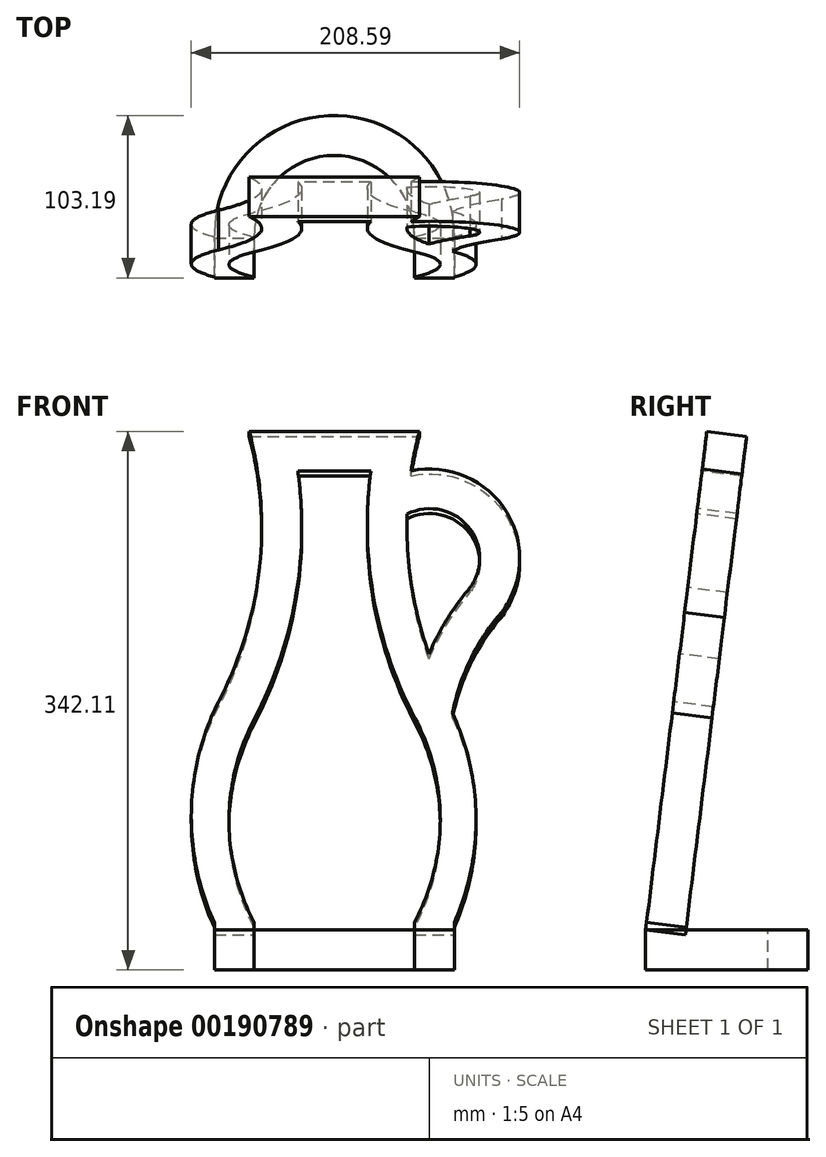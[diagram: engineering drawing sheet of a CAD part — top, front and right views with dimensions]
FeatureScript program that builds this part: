
annotation { "Feature Type Name" : "Feature", "Feature Type Description" : "" }
export const myFeature = defineFeature(function(context is Context, id is Id, definition is map)
    precondition{}
    {
        {
            var Q0;
            Q0=qCreatedBy(makeId("Top.planeOp"),FACE);
            var sketch = newSketch(context, id + "F0", { "sketchPlane" : qUnion([Q0])});
            skLineSegment(sketch, "E0", {"start": v(0, 0) * mm, "end": v(-62.54, 0) * mm});
            skSolve(sketch);
        }
        {
            var Q0;
            Q0=sQuery(id+"F0.wireOp",EDGE,"E0");
            var Q1;
            Q1=qCreatedBy(makeId("Front.planeOp"),FACE);
            cPlane(context, id + "F1", {"entities" : qUnion([Q0, Q1]), "cplaneType" : CPlaneType.LINE_ANGLE, "offset" : 25.4 * mm, "angle" : 7 * degree, "width" : 152.4 * mm, "height" : 152.4 * mm});
        }
        {
            var Q0;
            Q0=qCreatedBy(makeId("Top.planeOp"),FACE);
            cPlane(context, id + "F2", {"entities" : qUnion([Q0]), "cplaneType" : CPlaneType.OFFSET, "offset" : 0 * mm, "oppositeDirection" : true, "width" : 152.4 * mm, "height" : 152.4 * mm});
        }
        {
            var Q0;
            Q0=qCreatedBy(id+"F2.planeOp",FACE);
            var sketch = newSketch(context, id + "F3", { "sketchPlane" : qUnion([Q0])});
            skLineSegment(sketch, "E1", {"start": v(121.8, 0) * mm, "end": v(-111.18, 0) * mm, "construction": true});
            skLineSegment(sketch, "E2", {"start": v(0, 63.15) * mm, "end": v(0, -67.5) * mm, "construction": true});
            skLineSegment(sketch, "E3.bottom", {"start": v(-76.2, 0) * mm, "end": v(76.2, 0) * mm, "construction": true});
            skLineSegment(sketch, "E3.top", {"start": v(-76.2, 26.99) * mm, "end": v(76.2, 26.99) * mm, "construction": true});
            skLineSegment(sketch, "E3.left", {"start": v(-76.2, 0) * mm, "end": v(-76.2, 26.99) * mm});
            skLineSegment(sketch, "E3.right", {"start": v(76.2, 0) * mm, "end": v(76.2, 26.99) * mm});
            skPoint(sketch, "E4", {"position": v(0, 26.99) * mm});
            skLineSegment(sketch, "E5", {"start": v(-76.2, 0) * mm, "end": v(-50.8, 0) * mm});
            skLineSegment(sketch, "E6", {"start": v(-50.8, 0) * mm, "end": v(-50.8, 26.99) * mm});
            skLineSegment(sketch, "E7", {"start": v(76.2, 0) * mm, "end": v(50.8, 0) * mm});
            skLineSegment(sketch, "E8", {"start": v(50.8, 0) * mm, "end": v(50.8, 26.99) * mm});
            skArc(sketch, "E9", {"start": v(-50.8, 26.99) * mm, "mid": v(0, 77.79) * mm, "end": v(50.8, 26.99) * mm});
            skArc(sketch, "E10", {"start": v(-76.2, 26.99) * mm, "mid": v(0, 103.19) * mm, "end": v(76.2, 26.99) * mm});
            skSolve(sketch);
        }
        {
            var Q0;
            Q0=qSketchRegion(id+"F3",true);
            extrude(context, id + "F4", {"entities" : qUnion([Q0]), "oppositeDirection" : true, "depth" : 25.4 * mm});
        }
        {
            var Q0;
            Q0=qCreatedBy(id+"F1.planeOp",FACE);
            var sketch = newSketch(context, id + "F5", { "sketchPlane" : qUnion([Q0])});
            skArc(sketch, "E11", {"start": v(-63.5, 4.76) * mm, "mid": v(-78.79, 73.23) * mm, "end": v(-61.79, 141.29) * mm, "construction": true});
            skArc(sketch, "E12", {"start": v(-61.79, 141.29) * mm, "mid": v(-36, 221.84) * mm, "end": v(-38.1, 306.39) * mm, "construction": true});
            skLineSegment(sketch, "E13", {"start": v(-38.1, 306.39) * mm, "end": v(0, 306.39) * mm, "construction": true});
            skArc(sketch, "E14", {"start": v(-33.98, 274.64) * mm, "mid": v(-92.13, 270.54) * mm, "end": v(-96.22, 212.4) * mm, "construction": true});
            skLineSegment(sketch, "E15", {"start": v(-41.84, 266.78) * mm, "end": v(-126, 182.62) * mm, "construction": true});
            skArc(sketch, "E16", {"start": v(-96.22, 212.4) * mm, "mid": v(-74.32, 179.11) * mm, "end": v(-61.79, 141.29) * mm, "construction": true});
            skLineSegment(sketch, "E17.MirrorCS", {"start": v(38.1, 306.39) * mm, "end": v(0, 306.39) * mm, "construction": true});
            skArc(sketch, "E18.MirrorCS", {"start": v(61.79, 141.29) * mm, "mid": v(36, 221.84) * mm, "end": v(38.1, 306.39) * mm, "construction": true});
            skArc(sketch, "E19.MirrorCS", {"start": v(63.5, 4.76) * mm, "mid": v(78.79, 73.23) * mm, "end": v(61.79, 141.29) * mm, "construction": true});
            skArc(sketch, "E20.0", {"start": v(-76.2, 4.76) * mm, "mid": v(-90.04, 71.91) * mm, "end": v(-75.1, 138.83) * mm});
            skArc(sketch, "E20.1", {"start": v(-60.2, 176.74) * mm, "mid": v(-49, 220.83) * mm, "end": v(-46.27, 266.24) * mm});
            skArc(sketch, "E20.2", {"start": v(76.2, 4.76) * mm, "mid": v(90.8, 75.66) * mm, "end": v(73.66, 145.99) * mm});
            skArc(sketch, "E20.3", {"start": v(73.66, 145.99) * mm, "mid": v(47.67, 230.7) * mm, "end": v(54.02, 319.09) * mm});
            skLineSegment(sketch, "E20.4", {"start": v(54.02, 319.09) * mm, "end": v(0, 319.09) * mm});
            skLineSegment(sketch, "E20.5", {"start": v(-54.02, 319.09) * mm, "end": v(0, 319.09) * mm});
            skArc(sketch, "E21.0", {"start": v(-50.8, 4.76) * mm, "mid": v(-67.3, 70.02) * mm, "end": v(-51.37, 135.42) * mm});
            skArc(sketch, "E21.1", {"start": v(-51.37, 135.42) * mm, "mid": v(-25.08, 212.38) * mm, "end": v(-23.21, 293.69) * mm});
            skArc(sketch, "E21.2", {"start": v(50.8, 4.76) * mm, "mid": v(66.87, 69.44) * mm, "end": v(51.16, 134.2) * mm});
            skArc(sketch, "E21.3", {"start": v(51.16, 134.2) * mm, "mid": v(24.75, 211.77) * mm, "end": v(23.14, 293.69) * mm});
            skLineSegment(sketch, "E21.4", {"start": v(23.14, 293.69) * mm, "end": v(0, 293.69) * mm});
            skLineSegment(sketch, "E21.5", {"start": v(-23.21, 293.69) * mm, "end": v(0, 293.69) * mm});
            skArc(sketch, "E22.0", {"start": v(-106.05, 203.24) * mm, "mid": v(-86.38, 173.05) * mm, "end": v(-75.1, 138.83) * mm});
            skArc(sketch, "E23.0", {"start": v(-86.2, 219.1) * mm, "mid": v(-71.6, 198.91) * mm, "end": v(-60.2, 176.74) * mm});
            skArc(sketch, "E24.trimOffspring", {"start": v(-48.82, 293.84) * mm, "mid": v(-108.94, 268.44) * mm, "end": v(-106.05, 203.24) * mm});
            skArc(sketch, "E25.trimOffspring", {"start": v(-48.82, 293.84) * mm, "mid": v(-51.08, 306.53) * mm, "end": v(-54.02, 319.09) * mm});
            skArc(sketch, "E26.trimOffspring", {"start": v(-46.27, 266.24) * mm, "mid": v(-84.85, 258.44) * mm, "end": v(-86.2, 219.1) * mm});
            skLineSegment(sketch, "E27.bottom", {"start": v(76.2, 0) * mm, "end": v(50.8, 0) * mm});
            skLineSegment(sketch, "E27.top", {"start": v(76.2, 4.76) * mm, "end": v(50.8, 4.76) * mm, "construction": true});
            skLineSegment(sketch, "E27.left", {"start": v(76.2, 0) * mm, "end": v(76.2, 4.76) * mm});
            skLineSegment(sketch, "E27.right", {"start": v(50.8, 0) * mm, "end": v(50.8, 4.76) * mm});
            skLineSegment(sketch, "E28.bottom", {"start": v(-50.8, 0) * mm, "end": v(-76.2, 0) * mm});
            skLineSegment(sketch, "E28.top", {"start": v(-50.8, 4.76) * mm, "end": v(-76.2, 4.76) * mm, "construction": true});
            skLineSegment(sketch, "E28.left", {"start": v(-50.8, 0) * mm, "end": v(-50.8, 4.76) * mm});
            skLineSegment(sketch, "E28.right", {"start": v(-76.2, 0) * mm, "end": v(-76.2, 4.76) * mm});
            skPoint(sketch, "E29", {"position": v(-63.5, 4.76) * mm});
            skPoint(sketch, "E30", {"position": v(63.5, 4.76) * mm});
            skLineSegment(sketch, "E31", {"start": v(154.68, 351.94) * mm, "end": v(-310.06, 375.88) * mm});
            skPoint(sketch, "E32", {"position": v(-77.69, 363.91) * mm});
            skSolve(sketch);
        }
        {
            var Q0;
            Q0=qSketchRegion(id+"F5",true);
            extrude(context, id + "F6", {"entities" : qUnion([Q0]), "depth" : 25.4 * mm});
        }
    });
